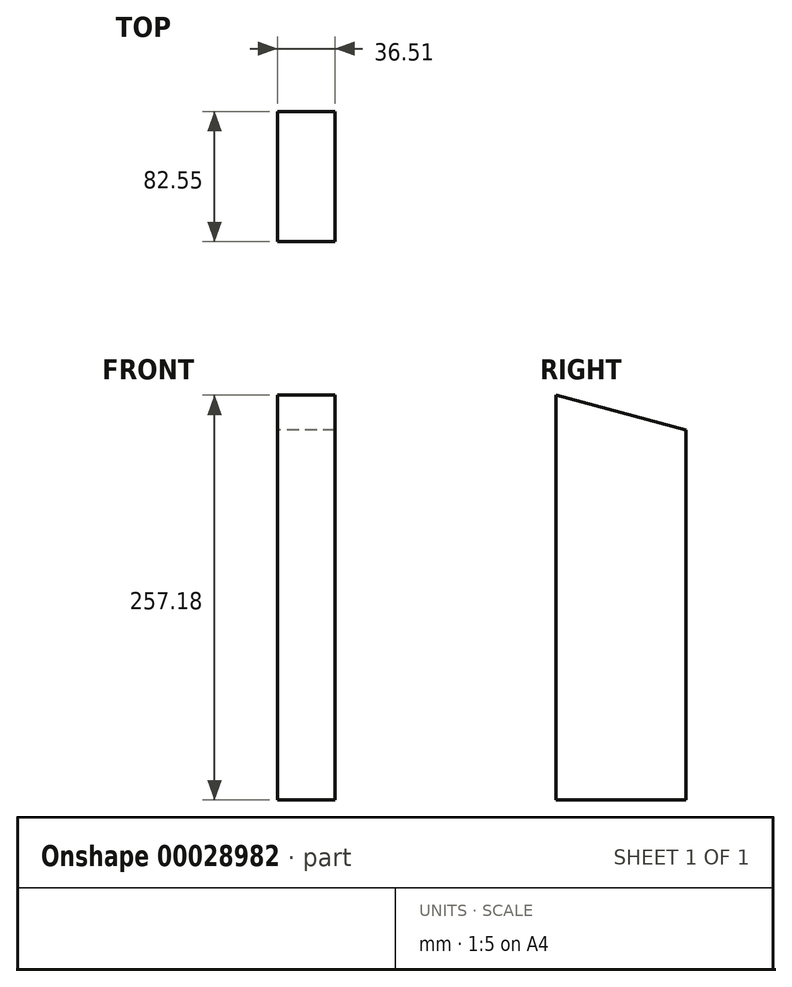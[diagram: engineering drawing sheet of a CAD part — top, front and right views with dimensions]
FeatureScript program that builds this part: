
annotation { "Feature Type Name" : "Feature", "Feature Type Description" : "" }
export const myFeature = defineFeature(function(context is Context, id is Id, definition is map)
    precondition{}
    {
        {
            var Q0;
            Q0=qCreatedBy(makeId("Right.planeOp"),FACE);
            var sketch = newSketch(context, id + "F0", { "sketchPlane" : qUnion([Q0])});
            skLineSegment(sketch, "E0", {"start": v(0, 0) * mm, "end": v(82.55, 0) * mm});
            skLineSegment(sketch, "E1", {"start": v(82.55, 0) * mm, "end": v(82.55, 234.95) * mm});
            skLineSegment(sketch, "E2", {"start": v(0, 0) * mm, "end": v(0, 257.18) * mm});
            skLineSegment(sketch, "E3", {"start": v(82.55, 234.95) * mm, "end": v(0, 257.18) * mm});
            skSolve(sketch);
        }
        {
            var Q0;
            Q0 = qSketchRegion(id + "F0", true);
            extrude(context, id + "F1", {"entities" : qUnion([Q0]), "depth" : 36.5 * mm});
        }
    });
